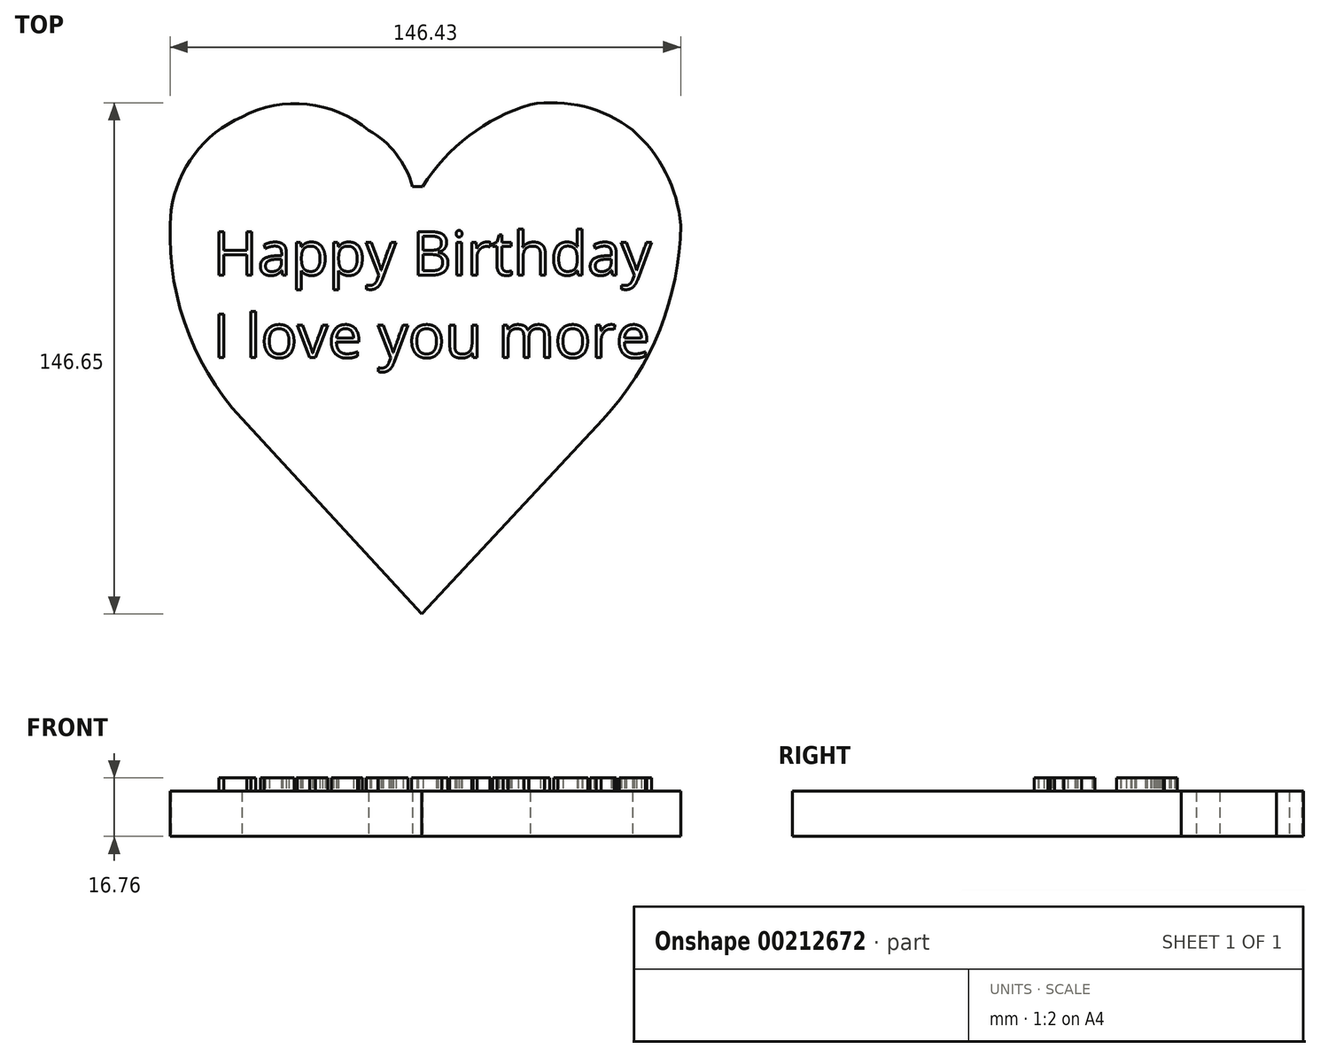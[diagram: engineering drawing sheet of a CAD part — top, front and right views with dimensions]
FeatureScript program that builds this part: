
annotation { "Feature Type Name" : "Feature", "Feature Type Description" : "" }
export const myFeature = defineFeature(function(context is Context, id is Id, definition is map)
    precondition{}
    {
        {
            var Q0;
            Q0=qCreatedBy(makeId("Top.planeOp"),FACE);
            var sketch = newSketch(context, id + "F0", { "sketchPlane" : qUnion([Q0])});
            skLineSegment(sketch, "E0", {"start": v(2.64, -78.33) * mm, "end": v(54.56, -22.56) * mm});
            skLineSegment(sketch, "E1", {"start": v(2.64, -78.33) * mm, "end": v(-49, -22.3) * mm});
            skArc(sketch, "E2", {"start": v(-69.24, 37.55) * mm, "mid": v(-65.47, 5.48) * mm, "end": v(-49, -22.3) * mm});
            skArc(sketch, "E3", {"start": v(-49, 64.25) * mm, "mid": v(-62.57, 53.52) * mm, "end": v(-69.24, 37.55) * mm});
            skArc(sketch, "E4", {"start": v(-12.62, 60.44) * mm, "mid": v(-30.23, 67.85) * mm, "end": v(-49, 64.25) * mm});
            skArc(sketch, "E5", {"start": v(0, 44.3) * mm, "mid": v(-4.71, 53.62) * mm, "end": v(-12.62, 60.44) * mm});
            skLineSegment(sketch, "E6", {"start": v(0, 44.3) * mm, "end": v(2.93, 44.3) * mm});
            skArc(sketch, "E7", {"start": v(33.73, 67.8) * mm, "mid": v(16.2, 58.84) * mm, "end": v(2.93, 44.3) * mm});
            skArc(sketch, "E8", {"start": v(63.07, 60.47) * mm, "mid": v(49.16, 67.19) * mm, "end": v(33.73, 67.8) * mm});
            skArc(sketch, "E9", {"start": v(76.86, 33.18) * mm, "mid": v(72.63, 48.18) * mm, "end": v(63.07, 60.47) * mm});
            skArc(sketch, "E10", {"start": v(54.56, -22.56) * mm, "mid": v(70.91, 3.23) * mm, "end": v(76.86, 33.18) * mm});
            skSolve(sketch);
        }
        {
            var Q0;
            Q0 = qSketchRegion(id + "F0", true);
            extrude(context, id + "F1", {"entities" : qUnion([Q0]), "depth" : 12.95 * mm});
        }
        {
            var Q0;
            Q0=makeQuery(id+"F1.opExtrude","CAP_FACE",FACE,{"disambiguationData":[OSD([sQuery(id+"F0.wireOp",EDGE,"E0"),sQuery(id+"F0.wireOp",EDGE,"E1"),sQuery(id+"F0.wireOp",EDGE,"E2"),sQuery(id+"F0.wireOp",EDGE,"E3"),sQuery(id+"F0.wireOp",EDGE,"E4"),sQuery(id+"F0.wireOp",EDGE,"E5"),sQuery(id+"F0.wireOp",EDGE,"E6"),sQuery(id+"F0.wireOp",EDGE,"E7"),sQuery(id+"F0.wireOp",EDGE,"E8"),sQuery(id+"F0.wireOp",EDGE,"E9"),sQuery(id+"F0.wireOp",EDGE,"E10")])],"isStart":false});
            var sketch = newSketch(context, id + "F2", { "sketchPlane" : qUnion([Q0])});
            skText(sketch, "E11", { "text": "Happy Birthday\nI love you more", "fontName": "OpenSans-Regular.ttf"});
            const initialGuessF2  = {"E11": [-0.0573, 0.01889, 1, 0, 0.01253]};
            skSetInitialGuess(sketch, initialGuessF2);
            skSolve(sketch);
        }
        {
            var Q0;
            Q0 = qSketchRegion(id + "F2", true);
            extrude(context, id + "F3", {"entities" : qUnion([Q0]), "operationType" : NewBodyOperationType.ADD, "depth" : 3.8 * mm});
        }
    });
